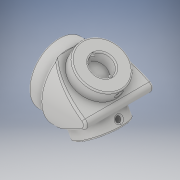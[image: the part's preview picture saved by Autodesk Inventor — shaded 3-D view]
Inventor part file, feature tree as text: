
AUTODESK INVENTOR PART (.ipt)
format: ipt  version: 2019 (Build 230136000, 136)  size: 530,944 bytes
history: native  units: in
note: dims shown in document units (in); Inventor stores cm internally (conversion verified against a paired STEP export)
features: sketch x16, extrude x8, fillet x6, plane x4, mirror x3, thread x2, sweep x1, projected_geometry x1
ambient origin geometry x8: Origin, YZ Plane, XZ Plane, XY Plane, X Axis, Y Axis, Z Axis, Center Point
bodies: Solid2 (feature_tree)
feature tree (41):
  extrude  "Extrusion6"  Depth=0.4724in TaperAngle=0.0deg
  extrude  "Extrusion7"  Depth=0.4724in TaperAngle=0.0deg
  sketch  "Sketch11"  dims[d34=0.0098in d35=45.0deg]
  extrude  "Extrusion9"  TaperAngle=45.0deg  [1 undecoded]
  sketch  "Sketch21"  dims[d70=3.1496in d71=0.0in d72=11.811in d73=0.0in d76=60.0deg]
  extrude  "Extrusion13"  TaperAngle=60.0deg  [1 undecoded]
  sketch  "Sketch26"  dims[d98=0.9449in d99=0.7874in d100=1.7323in d101=0.1417in d102=0.4724in d103=0.0in d104=0.2047in d105=0.315in d106=0.0in d107=0.3937in d108=0.0in d109=0.1969in]
  plane  "Work Plane5"
  extrude  "Extrusion15"  Depth=11.811in TaperAngle=0.0deg
  thread  "Thread3"  [1 undecoded]
  plane  "Work Plane7"
  mirror  "Mirror3"
  extrude  "Extrusion14"  Depth=0.4724in TaperAngle=0.0deg
  extrude  "Extrusion18"  Depth=2.5591in
  sketch  "Sketch36"  dims[d117=0.0472in]
  plane  "Work Plane10"
  extrude  "Extrusion19"  Depth=0.7874in
  thread  "Thread5"  [1 undecoded]
  plane  "Work Plane11"
  mirror  "Mirror6"
  mirror  "Mirror7"
  fillet  "Fillet3"  Radius=0.1417in
  fillet  "Fillet8"  Radius=0.4724in
  fillet  "Fillet9"  Radius=0.2047in
  fillet  "Fillet10"  Radius=0.315in
  fillet  "Fillet11"  Radius=0.3937in
  fillet  "Fillet14"  Radius=0.1969in
  sweep  "Sweep1"
  sketch  "3D Sketch2"
  sketch  "Sketch8"  dims[d28=0.0118in d29=0.4724in d30=0.0in]
  projected_geometry  "Projected Loop1"
  sketch  "Sketch9"  dims[d31=0.2362in d32=0.4724in d33=0.0in]
  sketch  "Sketch13"  dims[d42=0.1181in d43=0.0in d69=60.0deg]
  sketch  "Sketch22"  dims[d81=0.1969in d82=0.4724in d83=0.0in]
  sketch  "Sketch23"  dims[d84=0.3937in d85=0.0in d97=2.5591in]
  sketch  "Sketch28"  dims[d114=0.0472in d115=0.0472in]
  sketch  "Sketch34"  dims[d116=0.0472in]
  sketch  "Sketch37"  dims[d120=0.0in d121=0.0in]
  sketch  "3D Sketch3"
  sketch  "Sketch38"  dims[d122=0.1575in d125=0.0787in]
  sketch  "3D Sketch4"
note: 4 required parameter values undecoded (feature->parameter linkage not recoverable at this tier; creation-order binding heuristic only, values carry confidence <= 0.55)
